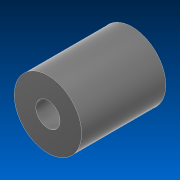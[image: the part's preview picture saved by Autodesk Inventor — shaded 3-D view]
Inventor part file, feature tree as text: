
AUTODESK INVENTOR PART (.ipt)
format: ipt  version: 2022.2 (Build 262287000, 287)  size: 88,064 bytes
history: native  units: in
note: dims shown in document units (in); Inventor stores cm internally (conversion verified against a paired STEP export)
features: extrude x1, sketch x1
ambient origin geometry x8: Origin, YZ Plane, XZ Plane, XY Plane, X Axis, Y Axis, Z Axis, Center Point
bodies: Solid1 (feature_tree)
feature tree (2):
  extrude  "Extrusion1"  Depth=0.625in
  sketch  "Sketch1"  dims[d0=0.18in d1=0.5in d2=0.625in d3=0.0in]
